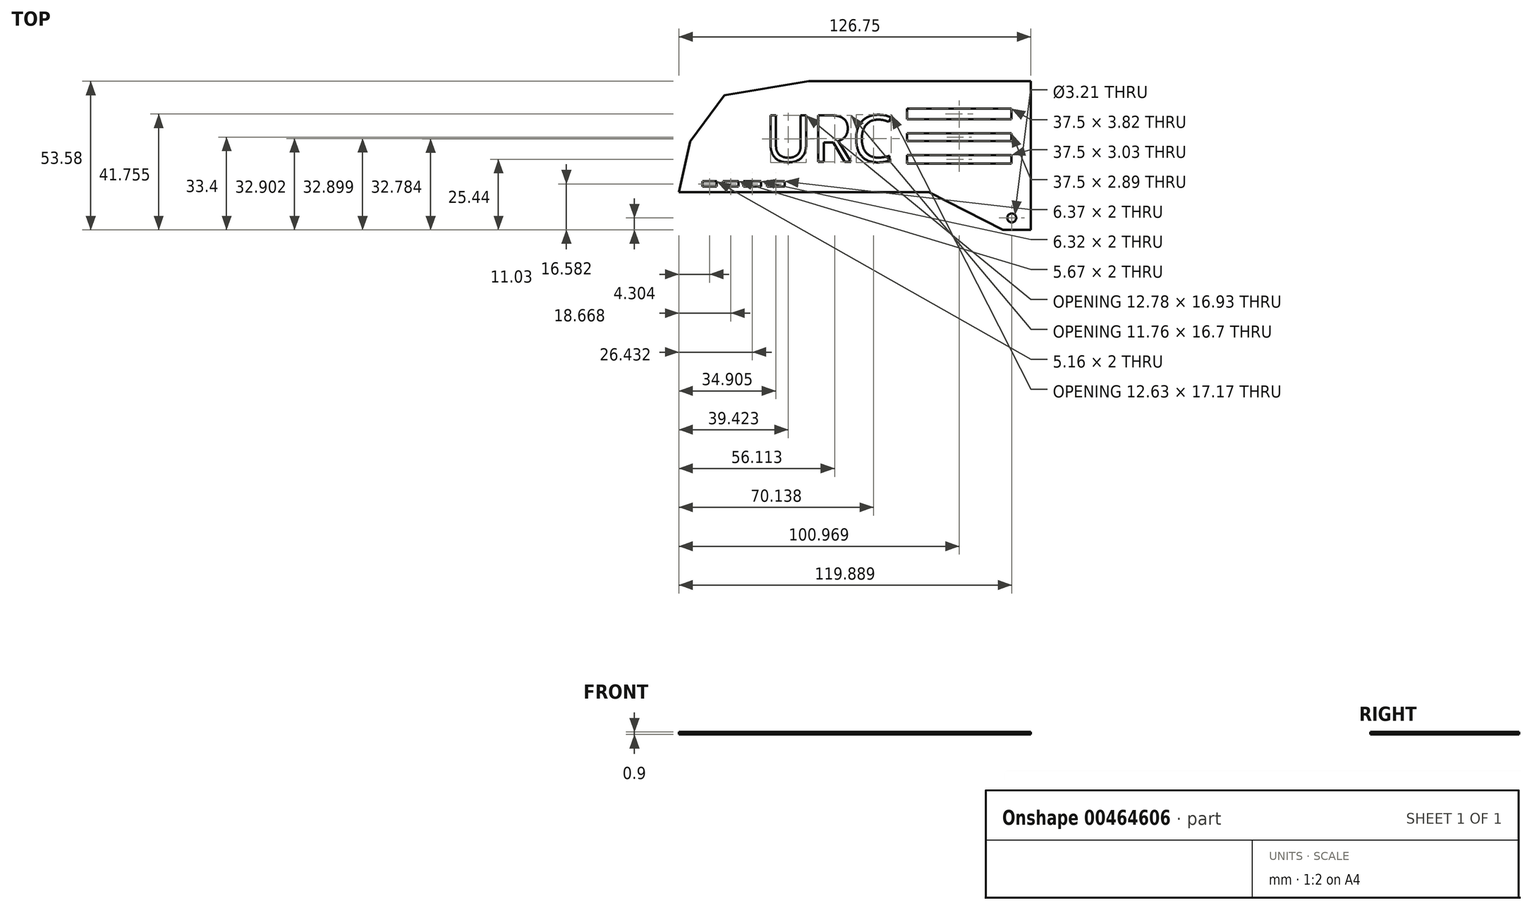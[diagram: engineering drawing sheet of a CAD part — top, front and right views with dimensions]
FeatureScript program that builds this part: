
annotation { "Feature Type Name" : "Feature", "Feature Type Description" : "" }
export const myFeature = defineFeature(function(context is Context, id is Id, definition is map)
    precondition{}
    {
        {
            var Q0;
            Q0=qCreatedBy(makeId("Top.planeOp"),FACE);
            var sketch = newSketch(context, id + "F0", { "sketchPlane" : qUnion([Q0])});
            skLineSegment(sketch, "E0", {"start": v(-60.4, -29.88) * mm, "end": v(29.6, -29.88) * mm});
            skLineSegment(sketch, "E1", {"start": v(29.6, -29.88) * mm, "end": v(56.34, -43.46) * mm});
            skLineSegment(sketch, "E2", {"start": v(56.34, -43.46) * mm, "end": v(66.34, -43.46) * mm});
            skLineSegment(sketch, "E3", {"start": v(66.34, -43.46) * mm, "end": v(66.34, 10.12) * mm});
            skLineSegment(sketch, "E4", {"start": v(66.34, 10.12) * mm, "end": v(-13.66, 10.12) * mm});
            skLineSegment(sketch, "E5", {"start": v(-13.66, 10.12) * mm, "end": v(-43.98, 5.12) * mm});
            skLineSegment(sketch, "E6", {"start": v(-43.98, 5.12) * mm, "end": v(-56.36, -11.55) * mm});
            skLineSegment(sketch, "E7", {"start": v(-56.36, -11.55) * mm, "end": v(-60.4, -29.88) * mm});
            skCircle(sketch, "E8", {"center": v(59.48, -39.16) * mm, "radius": 1.6 * mm});
            skText(sketch, "E9", { "text": "URC", "fontName": "OpenSans-Regular.ttf"});
            skLineSegment(sketch, "E10.bottom", {"start": v(-51.96, -25.88) * mm, "end": v(-22.32, -25.88) * mm});
            skLineSegment(sketch, "E10.top", {"start": v(-51.96, -27.88) * mm, "end": v(-22.32, -27.88) * mm});
            skLineSegment(sketch, "E10.left", {"start": v(-51.96, -25.88) * mm, "end": v(-51.96, -27.88) * mm});
            skLineSegment(sketch, "E10.right", {"start": v(-22.32, -25.88) * mm, "end": v(-22.32, -27.88) * mm});
            skLineSegment(sketch, "E11", {"start": v(-46.8, -25.88) * mm, "end": v(-46.8, -27.88) * mm});
            skLineSegment(sketch, "E12", {"start": v(-28.7, -25.88) * mm, "end": v(-28.7, -27.88) * mm});
            skLineSegment(sketch, "E13", {"start": v(-44.57, -25.88) * mm, "end": v(-44.57, -27.88) * mm});
            skLineSegment(sketch, "E14", {"start": v(-30.82, -25.88) * mm, "end": v(-30.82, -27.88) * mm});
            skLineSegment(sketch, "E15", {"start": v(-38.9, -25.88) * mm, "end": v(-38.9, -27.88) * mm});
            skLineSegment(sketch, "E16", {"start": v(-37.14, -25.88) * mm, "end": v(-37.14, -27.88) * mm});
            const initialGuessF0  = {"E9": [-0.0295, -0.01891, 1, 0, 0.01684]};
            skSetInitialGuess(sketch, initialGuessF0);
            skSolve(sketch);
        }
        {
            var Q0;
            Q0=makeQuery(id+"F0.imprint","IMPRINT",FACE,{"disambiguationData":[TD([[makeQuery(id+"F0.imprint","IMPRINT",EDGE,{"derivedFrom":sQuery(id+"F0.wireOp",EDGE,"E0")}),1.0]])]});
            var Q1;
            {var subQ0=sQuery(id+"F0.wireOp",EDGE,"E11");Q1=makeQuery(id+"F0.imprint","IMPRINT",FACE,{"disambiguationData":[TD([[makeQuery(id+"F0.imprint","IMPRINT",EDGE,{"derivedFrom":subQ0}),1.0]])]});}
            var Q2;
            {var subQ0=sQuery(id+"F0.wireOp",EDGE,"E15");Q2=makeQuery(id+"F0.imprint","IMPRINT",FACE,{"disambiguationData":[TD([[makeQuery(id+"F0.imprint","IMPRINT",EDGE,{"derivedFrom":subQ0}),1.0]])]});}
            var Q3;
            {var subQ0=sQuery(id+"F0.wireOp",EDGE,"E12");Q3=makeQuery(id+"F0.imprint","IMPRINT",FACE,{"disambiguationData":[TD([[makeQuery(id+"F0.imprint","IMPRINT",EDGE,{"derivedFrom":subQ0}),-1.0]])]});}
            extrude(context, id + "F1", {"entities" : qUnion([Q0, Q1, Q2, Q3]), "depth" : 0.9 * mm, "offsetDistance" : 25 * mm});
        }
        {
            var Q0;
            Q0=makeQuery(id+"F1.opExtrude","CAP_FACE",FACE,{"disambiguationData":[OSD([sQuery(id+"F0.wireOp",EDGE,"E0"),sQuery(id+"F0.wireOp",EDGE,"E1"),sQuery(id+"F0.wireOp",EDGE,"E2"),sQuery(id+"F0.wireOp",EDGE,"E3"),sQuery(id+"F0.wireOp",EDGE,"E4"),sQuery(id+"F0.wireOp",EDGE,"E5"),sQuery(id+"F0.wireOp",EDGE,"E6"),sQuery(id+"F0.wireOp",EDGE,"E7"),sQuery(id+"F0.wireOp",EDGE,"E8"),sQuery(id+"F0.wireOp",EDGE,"E9.sketch_text.stroke-0"),sQuery(id+"F0.wireOp",EDGE,"E9.sketch_text.stroke-1"),sQuery(id+"F0.wireOp",EDGE,"E9.sketch_text.stroke-2"),sQuery(id+"F0.wireOp",EDGE,"E9.sketch_text.stroke-3"),sQuery(id+"F0.wireOp",EDGE,"E9.sketch_text.stroke-4"),sQuery(id+"F0.wireOp",EDGE,"E9.sketch_text.stroke-5"),sQuery(id+"F0.wireOp",EDGE,"E9.sketch_text.stroke-6"),sQuery(id+"F0.wireOp",EDGE,"E9.sketch_text.stroke-7"),sQuery(id+"F0.wireOp",EDGE,"E9.sketch_text.stroke-8"),sQuery(id+"F0.wireOp",EDGE,"E9.sketch_text.stroke-9"),sQuery(id+"F0.wireOp",EDGE,"E9.sketch_text.stroke-10"),sQuery(id+"F0.wireOp",EDGE,"E9.sketch_text.stroke-11"),sQuery(id+"F0.wireOp",EDGE,"E9.sketch_text.stroke-12"),sQuery(id+"F0.wireOp",EDGE,"E9.sketch_text.stroke-13"),sQuery(id+"F0.wireOp",EDGE,"E9.sketch_text.stroke-14"),sQuery(id+"F0.wireOp",EDGE,"E9.sketch_text.stroke-15"),sQuery(id+"F0.wireOp",EDGE,"E9.sketch_text.stroke-16"),sQuery(id+"F0.wireOp",EDGE,"E9.sketch_text.stroke-17"),sQuery(id+"F0.wireOp",EDGE,"E9.sketch_text.stroke-18"),sQuery(id+"F0.wireOp",EDGE,"E9.sketch_text.stroke-19"),sQuery(id+"F0.wireOp",EDGE,"E9.sketch_text.stroke-20"),sQuery(id+"F0.wireOp",EDGE,"E9.sketch_text.stroke-21"),sQuery(id+"F0.wireOp",EDGE,"E9.sketch_text.stroke-22"),sQuery(id+"F0.wireOp",EDGE,"E9.sketch_text.stroke-23"),sQuery(id+"F0.wireOp",EDGE,"E9.sketch_text.stroke-24"),sQuery(id+"F0.wireOp",EDGE,"E9.sketch_text.stroke-32"),sQuery(id+"F0.wireOp",EDGE,"E9.sketch_text.stroke-33"),sQuery(id+"F0.wireOp",EDGE,"E9.sketch_text.stroke-34"),sQuery(id+"F0.wireOp",EDGE,"E9.sketch_text.stroke-35"),sQuery(id+"F0.wireOp",EDGE,"E9.sketch_text.stroke-36"),sQuery(id+"F0.wireOp",EDGE,"E9.sketch_text.stroke-37"),sQuery(id+"F0.wireOp",EDGE,"E9.sketch_text.stroke-38"),sQuery(id+"F0.wireOp",EDGE,"E9.sketch_text.stroke-39"),sQuery(id+"F0.wireOp",EDGE,"E9.sketch_text.stroke-40"),sQuery(id+"F0.wireOp",EDGE,"E9.sketch_text.stroke-41"),sQuery(id+"F0.wireOp",EDGE,"E9.sketch_text.stroke-42"),sQuery(id+"F0.wireOp",EDGE,"E9.sketch_text.stroke-43"),sQuery(id+"F0.wireOp",EDGE,"E9.sketch_text.stroke-44"),sQuery(id+"F0.wireOp",EDGE,"E9.sketch_text.stroke-45"),sQuery(id+"F0.wireOp",EDGE,"E9.sketch_text.stroke-46"),sQuery(id+"F0.wireOp",EDGE,"E10.bottom"),sQuery(id+"F0.wireOp",EDGE,"E10.top"),sQuery(id+"F0.wireOp",EDGE,"E10.left"),sQuery(id+"F0.wireOp",EDGE,"E10.right"),sQuery(id+"F0.wireOp",EDGE,"E11"),sQuery(id+"F0.wireOp",EDGE,"E12"),sQuery(id+"F0.wireOp",EDGE,"E13"),sQuery(id+"F0.wireOp",EDGE,"E14"),sQuery(id+"F0.wireOp",EDGE,"E15"),sQuery(id+"F0.wireOp",EDGE,"E16")])],"isStart":false});
            var sketch = newSketch(context, id + "F2", { "sketchPlane" : qUnion([Q0])});
            skLineSegment(sketch, "E17", {"start": v(66.34, -34.4) * mm, "end": v(38.5, -34.4) * mm});
            skSolve(sketch);
        }
        {
            var Q0;
            {var subQ0=sQuery(id+"F2.wireOp",EDGE,"E17");Q0=makeQuery(id+"F2.imprint","IMPRINT",FACE,{"disambiguationData":[TD([[makeQuery(id+"F2.imprint","IMPRINT",EDGE,{"derivedFrom":subQ0}),-1.0]])]});}
            var sketch = newSketch(context, id + "F3", { "sketchPlane" : qUnion([Q0])});
            skLineSegment(sketch, "E18", {"start": v(21.8, 5.2) * mm, "end": v(21.8, -25.06) * mm});
            skLineSegment(sketch, "E19", {"start": v(59.3, 4.28) * mm, "end": v(59.3, -30.32) * mm});
            skLineSegment(sketch, "E20.bottom", {"start": v(21.8, 5.2) * mm, "end": v(59.3, 5.2) * mm});
            skLineSegment(sketch, "E20.top", {"start": v(21.8, 0.2) * mm, "end": v(59.3, 0.2) * mm});
            skLineSegment(sketch, "E20.left", {"start": v(21.8, 5.2) * mm, "end": v(21.8, 0.2) * mm});
            skLineSegment(sketch, "E20.right", {"start": v(59.3, 5.2) * mm, "end": v(59.3, 0.2) * mm});
            skLineSegment(sketch, "E21.bottom", {"start": v(21.8, -3.61) * mm, "end": v(59.3, -3.61) * mm});
            skLineSegment(sketch, "E21.top", {"start": v(21.8, -8.61) * mm, "end": v(59.3, -8.61) * mm});
            skLineSegment(sketch, "E21.left", {"start": v(21.8, -3.61) * mm, "end": v(21.8, -8.61) * mm});
            skLineSegment(sketch, "E21.right", {"start": v(59.3, -3.61) * mm, "end": v(59.3, -8.61) * mm});
            skLineSegment(sketch, "E22.bottom", {"start": v(21.8, -11.5) * mm, "end": v(59.3, -11.5) * mm});
            skLineSegment(sketch, "E22.top", {"start": v(21.8, -16.5) * mm, "end": v(59.3, -16.5) * mm});
            skLineSegment(sketch, "E22.left", {"start": v(21.8, -11.5) * mm, "end": v(21.8, -16.5) * mm});
            skLineSegment(sketch, "E22.right", {"start": v(59.3, -11.5) * mm, "end": v(59.3, -16.5) * mm});
            skLineSegment(sketch, "E23.bottom", {"start": v(21.8, -19.53) * mm, "end": v(59.3, -19.53) * mm});
            skLineSegment(sketch, "E23.top", {"start": v(21.8, -24.53) * mm, "end": v(59.3, -24.53) * mm});
            skLineSegment(sketch, "E23.left", {"start": v(21.8, -19.53) * mm, "end": v(21.8, -24.53) * mm});
            skLineSegment(sketch, "E23.right", {"start": v(59.3, -19.53) * mm, "end": v(59.3, -24.53) * mm});
            skSolve(sketch);
        }
        {
            var Q0;
            {var subQ0=sQuery(id+"F3.wireOp",EDGE,"E20.top");Q0=makeQuery(id+"F3.imprint","IMPRINT",FACE,{"disambiguationData":[TD([[makeQuery(id+"F3.imprint","IMPRINT",EDGE,{"derivedFrom":subQ0}),-1.0]])]});}
            var Q1;
            {var subQ0=sQuery(id+"F3.wireOp",EDGE,"E22.top");Q1=makeQuery(id+"F3.imprint","IMPRINT",FACE,{"disambiguationData":[TD([[makeQuery(id+"F3.imprint","IMPRINT",EDGE,{"derivedFrom":subQ0}),-1.0]])]});}
            var Q2;
            {var subQ0=sQuery(id+"F3.wireOp",EDGE,"E21.top");Q2=makeQuery(id+"F3.imprint","IMPRINT",FACE,{"disambiguationData":[TD([[makeQuery(id+"F3.imprint","IMPRINT",EDGE,{"derivedFrom":subQ0}),-1.0]])]});}
            extrude(context, id + "F4", {"entities" : qUnion([Q0, Q1, Q2]), "operationType" : NewBodyOperationType.REMOVE, "endBound" : BoundingType.UP_TO_NEXT, "oppositeDirection" : true, "depth" : 25 * mm, "offsetDistance" : 25 * mm});
        }
    });
